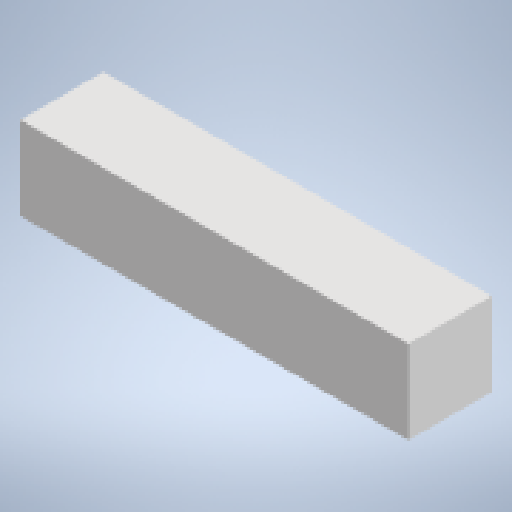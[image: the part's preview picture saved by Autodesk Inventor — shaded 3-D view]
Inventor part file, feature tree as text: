
AUTODESK INVENTOR PART (.ipt)
format: ipt  version: 2024 (Build 280153000, 153)  size: 122,368 bytes
history: native  units: mm
features: extrude x1, sketch x1
ambient origin geometry x8: Origin, YZ Plane, XZ Plane, XY Plane, X Axis, Y Axis, Z Axis, Center Point
bodies: Solid1 (feature_tree)
feature tree (2):
  extrude  "Extrusion1"  Depth=45.0mm
  sketch  "Sketch2"  dims[d0=45.0mm d1=45.0mm d2=210.0mm d3=0.0mm]
